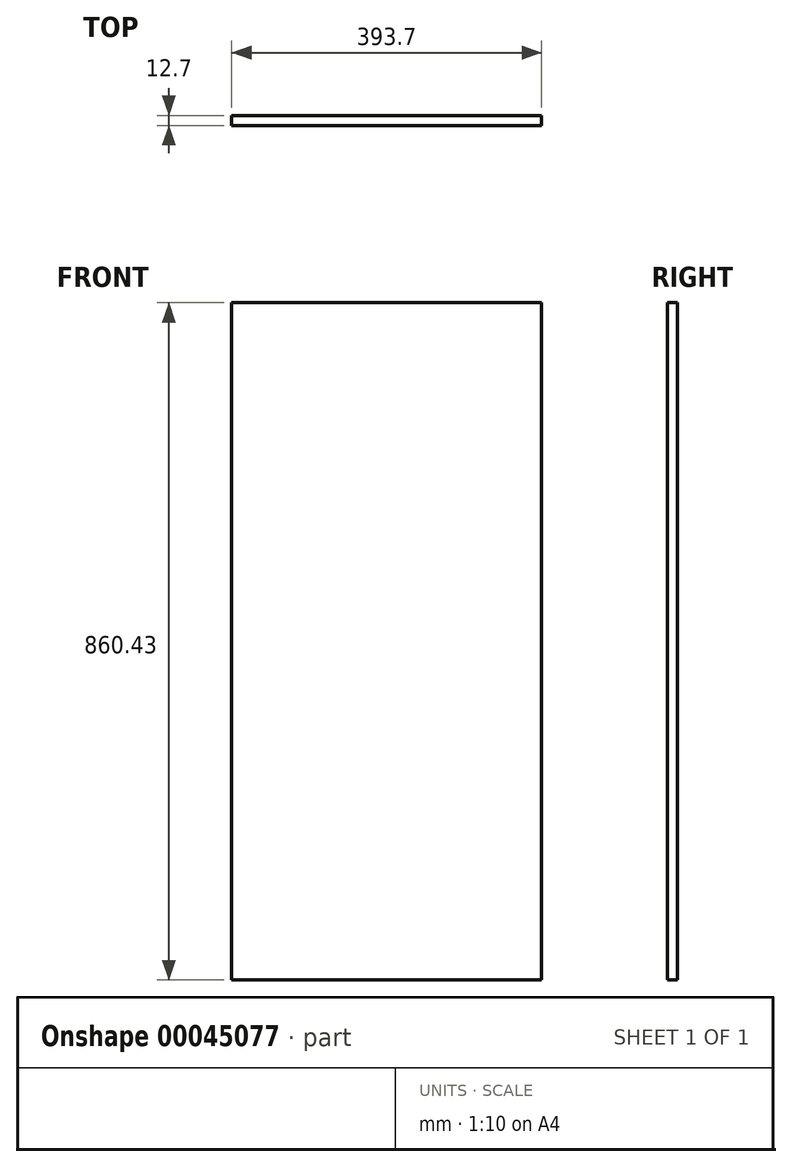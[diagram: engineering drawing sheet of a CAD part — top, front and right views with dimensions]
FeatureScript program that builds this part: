
annotation { "Feature Type Name" : "Feature", "Feature Type Description" : "" }
export const myFeature = defineFeature(function(context is Context, id is Id, definition is map)
    precondition{}
    {
        {
            var Q0;
            Q0=qCreatedBy(makeId("Front.planeOp"),FACE);
            var sketch = newSketch(context, id + "F0", { "sketchPlane" : qUnion([Q0])});
            skLineSegment(sketch, "E0.bottom", {"start": v(-22.16, 925.68) * mm, "end": v(371.54, 925.68) * mm});
            skLineSegment(sketch, "E0.top", {"start": v(-22.16, 65.25) * mm, "end": v(371.54, 65.25) * mm});
            skLineSegment(sketch, "E0.left", {"start": v(-22.16, 925.68) * mm, "end": v(-22.16, 65.25) * mm});
            skLineSegment(sketch, "E0.right", {"start": v(371.54, 925.68) * mm, "end": v(371.54, 65.25) * mm});
            skLineSegment(sketch, "E1", {"start": v(-22.16, 116.05) * mm, "end": v(371.54, 116.05) * mm, "construction": true});
            skSolve(sketch);
        }
        {
            var Q0;
            Q0=makeQuery(id+"F0.imprint","IMPRINT",FACE,{"disambiguationData":[TD([[makeQuery(id+"F0.imprint","IMPRINT",EDGE,{"derivedFrom":sQuery(id+"F0.wireOp",EDGE,"E0.bottom")}),-1.0]])]});
            extrude(context, id + "F1", {"entities" : qUnion([Q0]), "depth" : 12.7 * mm});
        }
    });
